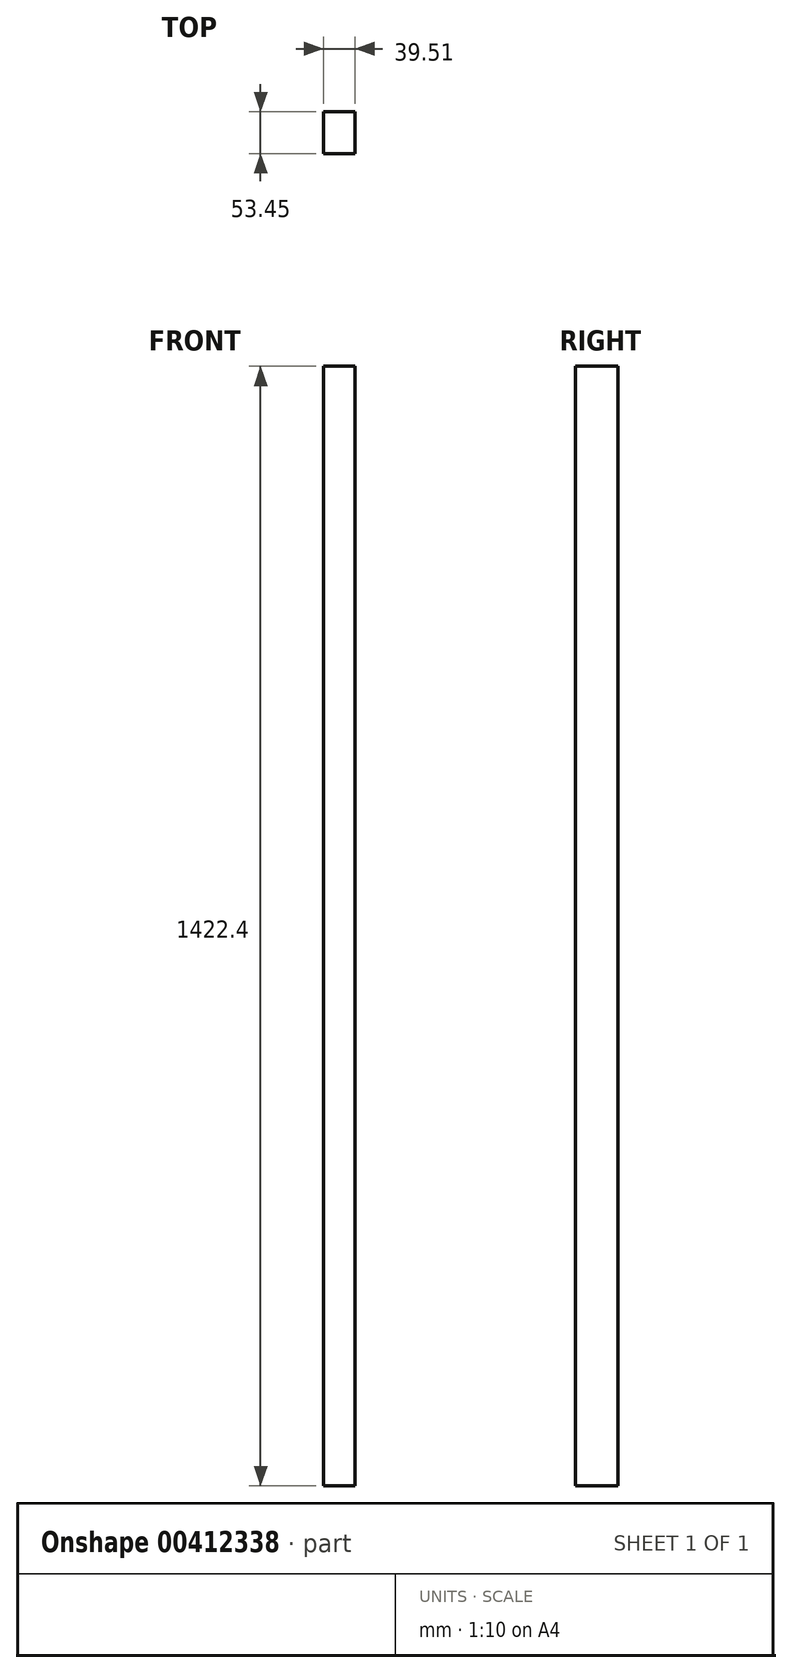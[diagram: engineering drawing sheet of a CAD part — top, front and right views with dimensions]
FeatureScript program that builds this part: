
annotation { "Feature Type Name" : "Feature", "Feature Type Description" : "" }
export const myFeature = defineFeature(function(context is Context, id is Id, definition is map)
    precondition{}
    {
        {
            var Q0;
            Q0=qCreatedBy(makeId("Top.planeOp"),FACE);
            var sketch = newSketch(context, id + "F0", { "sketchPlane" : qUnion([Q0])});
            skLineSegment(sketch, "E0.bottom", {"start": v(0, 0) * mm, "end": v(-39.5, 0) * mm});
            skLineSegment(sketch, "E0.top", {"start": v(0, -53.45) * mm, "end": v(-39.5, -53.45) * mm});
            skLineSegment(sketch, "E0.left", {"start": v(0, 0) * mm, "end": v(0, -53.45) * mm});
            skLineSegment(sketch, "E0.right", {"start": v(-39.5, 0) * mm, "end": v(-39.5, -53.45) * mm});
            skSolve(sketch);
        }
        {
            var Q0;
            Q0=makeQuery(id+"F0.imprint","IMPRINT",FACE,{"disambiguationData":[TD([[makeQuery(id+"F0.imprint","IMPRINT",EDGE,{"derivedFrom":sQuery(id+"F0.wireOp",EDGE,"E0.bottom")}),1.0]])]});
            extrude(context, id + "F1", {"entities" : qUnion([Q0]), "depth" : 1422.4 * mm});
        }
    });
